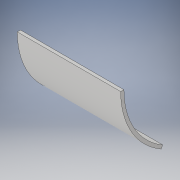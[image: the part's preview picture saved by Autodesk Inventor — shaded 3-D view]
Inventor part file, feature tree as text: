
AUTODESK INVENTOR PART (.ipt)
format: ipt  version: 2019 (Build 230136000, 136)  size: 96,256 bytes
history: native  units: in
note: dims shown in document units (in); Inventor stores cm internally (conversion verified against a paired STEP export)
features: revolve x1, sketch x1
ambient origin geometry x8: Origin, YZ Plane, XZ Plane, XY Plane, X Axis, Y Axis, Z Axis, Center Point
bodies: Solid1 (feature_tree)
feature tree (2):
  revolve  "Revolution1"  [1 undecoded]
  sketch  "Sketch1"  dims[d0=4.0in d1=0.125in d2=3.0in d3=60.0deg]
note: 1 required parameter value undecoded (feature->parameter linkage not recoverable at this tier; creation-order binding heuristic only, values carry confidence <= 0.55)
